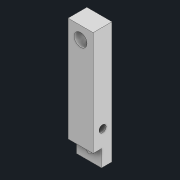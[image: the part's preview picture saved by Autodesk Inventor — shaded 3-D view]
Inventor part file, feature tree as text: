
AUTODESK INVENTOR PART (.ipt)
format: ipt  version: 2022 (Build 260153000, 153)  size: 112,640 bytes
history: native  units: mm
features: sketch x5, extrude x3, hole x2
ambient origin geometry x8: Origin, YZ Plane, XZ Plane, XY Plane, X Axis, Y Axis, Z Axis, Center Point
bodies: Body1 (feature_tree)
feature tree (10):
  extrude  "押し出し3"  Depth=30.0mm
  extrude  "押し出し4"  Depth=125.0mm
  hole  "穴2"  [1 undecoded]
  extrude  "押し出し5"  Depth=30.0mm
  hole  "穴3"  [1 undecoded]
  sketch  "スケッチ5"
  sketch  "スケッチ6"
  sketch  "スケッチ7"
  sketch  "スケッチ8"
  sketch  "スケッチ9"
note: 2 required parameter values undecoded (feature->parameter linkage not recoverable at this tier; creation-order binding heuristic only, values carry confidence <= 0.55)
